# Revit family: Pablo-IP_55-Plain_Door-syst-NoHosted-IT-en
name_source: partatom
category: Electrical Equipment
units: mm (PartAtom-declared; Revit-internal decimal feet)

## family parameters
Always vertical = Yes
Cut with Voids When Loaded = No
Panel Configuration = Two Columns, Circuits Across
Part Type = Panelboard
Room Calculation Point = No
Round Connector Dimension = Use Diameter
Shared = No
Work Plane-Based = Yes

## types (3) — shared parameters
Default Elevation = 1219 mm
EF000003 - Mounting method = EV000384 - Surface mounted (plaster)
EF000008 - Width = 195 mm  [stored 0.639764 ft]
EF000118 - With mounting plate = No
EF000266 - Number of rows = 1
EF000339 - Type of cover = EV001012 - Cover
EF001062 - EMC-version = No
EF001088 - Extension possible = No
EF005474 - Degree of protection (IP) = EV006420 - IP55
EF006244 - Transparent cover/door = No
EF009212 - Cover model = EV009916 - With notch
EF015776 - Earthing terminal block = No
EF015777 - Neutral terminal block = No
EF015941 - Signal passing door = No
HG000001 - Number of columns = 1
HG000002 - With door or cover = Yes
HG000003 - Range = Pablo
HG000005 - Thickness = 3 mm  [stored 0.00984252 ft]
HG000006 - Flush mounted = No
HG000009 - Double swing door = No
HG000010 - Asymmetric doors = No
HG000011 - Empty rows from bottom = No
Manufacturer = Hager
Type Comments = Pablo
zero-valued in all types: EF000332 - Built-in height, EF000846 - Built-in width, HG000007 - Number of empty columns, HG000008 - Number of empty rows

## per-type parameters (varying)
| type | EF000007 - Colour | EF000040 - Height | EF000049 - Depth | EF000116 - RAL-number | EF000218 - Built-in depth | EF001131 - Internal depth | EF001134 - DIN-rail | EF001596 - Material housing | EF002950 - Width in number of modular spacings | EF004462 - Type of closure | EF006306 - With lock | HG000004 - Manufacturer reference | Model |
| Surface mounted IP55 W195 H128 D103 4 Modular spacings - B05762 | EV000233 - Red | 128 mm | 103 mm | 3000 | 80 mm | 103 mm | No | EV000139 - Plastic | 4 | 0 | Yes | B05762 | B05762 |
| Surface mounted IP55 W195 H200 D106 8 Modular spacings - B05764 | 0 | 200 mm  [stored 0.656168 ft] | 106 mm  [stored 0.347769 ft] | 0 | 0 mm  [stored 0 ft] | 0 mm  [stored 0 ft] | Yes | 0 | 8 | EV000154 - Other | No | B05764 | B05764 |
| Surface mounted IP55 W195 H200 D106 8 Modular spacings - B05766 | 0 | 200 mm  [stored 0.656168 ft] | 106 mm  [stored 0.347769 ft] | 0 | 0 mm  [stored 0 ft] | 0 mm  [stored 0 ft] | Yes | 0 | 8 | EV000154 - Other | No | B05766 | B05766 |

note: [stored X ft] marks values corroborated as IEEE doubles in the binary element streams (Revit-internal decimal feet)

## geometry (parser evidence)
native form markers: Sweep x16
no freeform markers — native parametric forms only
